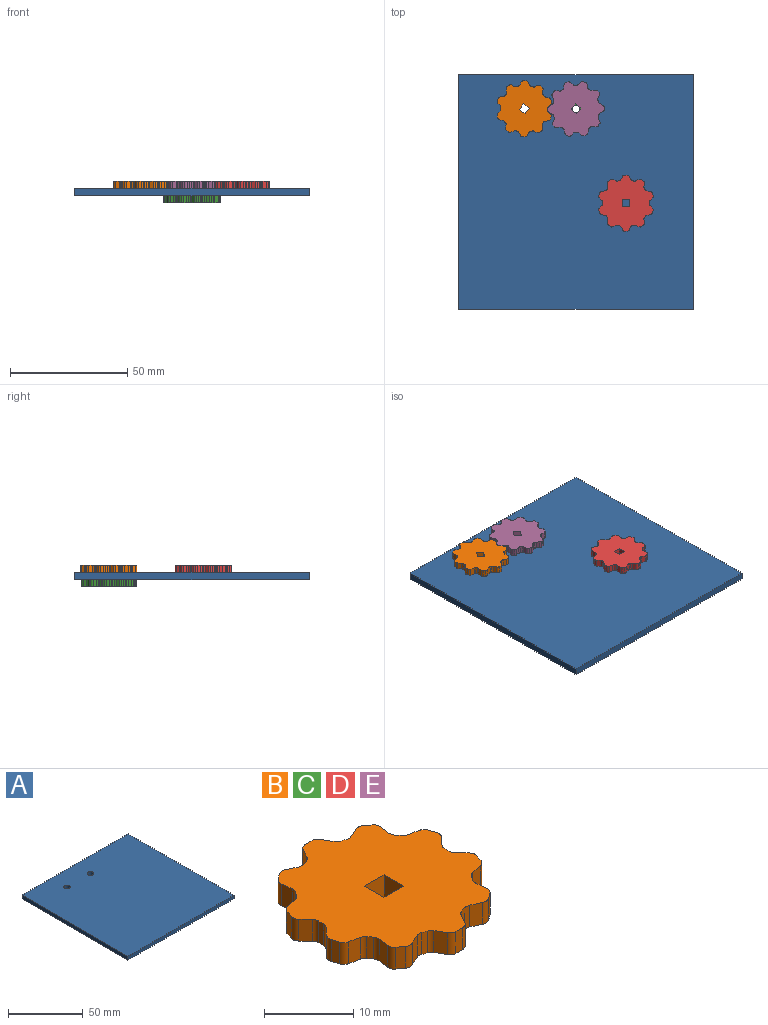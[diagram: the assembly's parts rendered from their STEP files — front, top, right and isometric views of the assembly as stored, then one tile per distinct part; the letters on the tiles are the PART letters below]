
ASSEMBLY  parts=5 mates=3
PART A: 8 faces, bbox 100x100x3 mm
  f0: plane 100x3mm, normal (1,0,0), area 300mm2, adj f1,f3,f4,f5
  f1: plane 100x3mm, normal (0,1,0), area 300mm2, adj f0,f2,f4,f5
  f2: plane 100x3mm, normal (-1,0,0), area 300mm2, adj f1,f3,f4,f5
  f3: plane 100x3mm, normal (0,-1,0), area 300mm2, adj f0,f2,f4,f5
  f4: plane 100x100mm, normal (0,0,1), area 9969.8mm2, adj f0,f1,f2,f3,f6,f7
  f5: plane 100x100mm, normal (0,0,-1), area 9969.8mm2, adj f0,f1,f2,f3,f6,f7
  f6: cylinder r=2.19mm len=4.38mm, axis (0,0,1), area 41.3mm2, adj f4,f5
  f7: cylinder r=2.19mm len=4.38mm, axis (0,0,1), area 41.3mm2, adj f4,f5
PART B: 86 faces, bbox 23.2x23.9x3 mm
  f0: cylinder r=10mm len=3mm, axis (0,0,-1), area 2.1mm2, adj f14,f15,f20,f84
  f1: cylinder r=10mm len=3mm, axis (0,0,-1), area 2.1mm2, adj f14,f15,f77,f83
  f2: cylinder r=10mm len=3mm, axis (0,0,-1), area 2.1mm2, adj f14,f15,f70,f76
  f3: cylinder r=10mm len=3mm, axis (0,0,-1), area 2.1mm2, adj f14,f15,f63,f69
  f4: cylinder r=10mm len=3mm, axis (0,0,-1), area 2.1mm2, adj f14,f15,f56,f62
  f5: cylinder r=10mm len=3mm, axis (0,0,-1), area 2.1mm2, adj f14,f15,f49,f55
  f6: cylinder r=10mm len=3mm, axis (0,0,-1), area 2.1mm2, adj f14,f15,f42,f48
  f7: cylinder r=10mm len=3mm, axis (0,0,-1), area 2.1mm2, adj f14,f15,f35,f41
  f8: cylinder r=10mm len=3mm, axis (0,0,-1), area 2.1mm2, adj f14,f15,f28,f34
  f9: cylinder r=10mm len=3mm, axis (0,0,-1), area 2.1mm2, adj f14,f15,f21,f27
  f10: plane 3.05x3mm, normal (0,-1,0), area 9.2mm2, adj f11,f13,f14,f15
  f11: plane 3.05x3mm, normal (-1,0,0), area 9.2mm2, adj f10,f12,f14,f15
  f12: plane 3.05x3mm, normal (0,1,0), area 9.2mm2, adj f11,f13,f14,f15
  f13: plane 3.05x3mm, normal (1,0,0), area 9.2mm2, adj f10,f12,f14,f15
  f14: plane 23.9x23.15mm, normal (0,0,1), area 372.8mm2, adj f0,f1,f2,f3,f4,f5,f6,f7
  f15: plane 23.9x23.15mm, normal (0,0,-1), area 372.8mm2, adj f0,f1,f2,f3,f4,f5,f6,f7
  f16: plane 3x1.06mm, normal (0,1,0), area 3.2mm2, adj f14,f15,f19,f22
  f17: plane 3x1.35mm, normal (-0.87,0.49,0), area 4.6mm2, adj f14,f15,f19,f20
  f18: plane 3x1.35mm, normal (0.87,0.49,0), area 4.6mm2, adj f14,f15,f21,f22
  f19: cylinder r=1mm len=3mm, axis (0,0,1), area 3.2mm2, adj f14,f15,f16,f17
  f20: cylinder r=1mm len=3mm, axis (0,0,-1), area 2.3mm2, adj f0,f14,f15,f17
  f21: cylinder r=1mm len=3mm, axis (0,0,-1), area 2.3mm2, adj f9,f14,f15,f18
  f22: cylinder r=1mm len=3mm, axis (0,0,-1), area 3.2mm2, adj f14,f15,f16,f18
  f23: plane 3x0.86mm, normal (0.59,0.81,0), area 3.2mm2, adj f14,f15,f26,f29
  f24: plane 3x1.4mm, normal (-0.42,0.91,0), area 4.6mm2, adj f14,f15,f26,f27
  f25: plane 3x1.53mm, normal (0.99,-0.12,0), area 4.6mm2, adj f14,f15,f28,f29
  f26: cylinder r=1mm len=3mm, axis (0,0,1), area 3.2mm2, adj f14,f15,f23,f24
  f27: cylinder r=1mm len=3mm, axis (0,0,-1), area 2.3mm2, adj f9,f14,f15,f24
  f28: cylinder r=1mm len=3mm, axis (0,0,-1), area 2.3mm2, adj f8,f14,f15,f25
  f29: cylinder r=1mm len=3mm, axis (0,0,-1), area 3.2mm2, adj f14,f15,f23,f25
  f30: plane 3x1.01mm, normal (0.95,0.31,0), area 3.2mm2, adj f14,f15,f33,f36
  f31: plane 3x1.51mm, normal (0.19,0.98,0), area 4.6mm2, adj f14,f15,f33,f34
  f32: plane 3x1.13mm, normal (0.73,-0.68,0), area 4.6mm2, adj f14,f15,f35,f36
  f33: cylinder r=1mm len=3mm, axis (0,0,1), area 3.2mm2, adj f14,f15,f30,f31
  f34: cylinder r=1mm len=3mm, axis (0,0,-1), area 2.3mm2, adj f8,f14,f15,f31
  f35: cylinder r=1mm len=3mm, axis (0,0,-1), area 2.3mm2, adj f7,f14,f15,f32
  f36: cylinder r=1mm len=3mm, axis (0,0,-1), area 3.2mm2, adj f14,f15,f30,f32
  f37: plane 3x1.01mm, normal (0.95,-0.31,0), area 3.2mm2, adj f14,f15,f40,f43
  f38: plane 3x1.13mm, normal (0.73,0.68,0), area 4.6mm2, adj f14,f15,f40,f41
  f39: plane 3x1.51mm, normal (0.19,-0.98,0), area 4.6mm2, adj f14,f15,f42,f43
  f40: cylinder r=1mm len=3mm, axis (0,0,1), area 3.2mm2, adj f14,f15,f37,f38
  f41: cylinder r=1mm len=3mm, axis (0,0,-1), area 2.3mm2, adj f7,f14,f15,f38
  f42: cylinder r=1mm len=3mm, axis (0,0,-1), area 2.3mm2, adj f6,f14,f15,f39
  f43: cylinder r=1mm len=3mm, axis (0,0,-1), area 3.2mm2, adj f14,f15,f37,f39
  f44: plane 3x0.86mm, normal (0.59,-0.81,0), area 3.2mm2, adj f14,f15,f47,f50
  f45: plane 3x1.53mm, normal (0.99,0.12,0), area 4.6mm2, adj f14,f15,f47,f48
  f46: plane 3x1.4mm, normal (-0.42,-0.91,0), area 4.6mm2, adj f14,f15,f49,f50
  f47: cylinder r=1mm len=3mm, axis (0,0,1), area 3.2mm2, adj f14,f15,f44,f45
  f48: cylinder r=1mm len=3mm, axis (0,0,-1), area 2.3mm2, adj f6,f14,f15,f45
  f49: cylinder r=1mm len=3mm, axis (0,0,-1), area 2.3mm2, adj f5,f14,f15,f46
  f50: cylinder r=1mm len=3mm, axis (0,0,-1), area 3.2mm2, adj f14,f15,f44,f46
  f51: plane 3x1.06mm, normal (0,-1,0), area 3.2mm2, adj f14,f15,f54,f57
  f52: plane 3x1.35mm, normal (0.87,-0.49,0), area 4.6mm2, adj f14,f15,f54,f55
  f53: plane 3x1.35mm, normal (-0.87,-0.49,0), area 4.6mm2, adj f14,f15,f56,f57
  f54: cylinder r=1mm len=3mm, axis (0,0,1), area 3.2mm2, adj f14,f15,f51,f52
  f55: cylinder r=1mm len=3mm, axis (0,0,-1), area 2.3mm2, adj f5,f14,f15,f52
  f56: cylinder r=1mm len=3mm, axis (0,0,-1), area 2.3mm2, adj f4,f14,f15,f53
  f57: cylinder r=1mm len=3mm, axis (0,0,-1), area 3.2mm2, adj f14,f15,f51,f53
  f58: plane 3x0.86mm, normal (-0.59,-0.81,0), area 3.2mm2, adj f14,f15,f61,f64
  f59: plane 3x1.4mm, normal (0.42,-0.91,0), area 4.6mm2, adj f14,f15,f61,f62
  f60: plane 3x1.53mm, normal (-0.99,0.12,0), area 4.6mm2, adj f14,f15,f63,f64
  f61: cylinder r=1mm len=3mm, axis (0,0,1), area 3.2mm2, adj f14,f15,f58,f59
  f62: cylinder r=1mm len=3mm, axis (0,0,-1), area 2.3mm2, adj f4,f14,f15,f59
  f63: cylinder r=1mm len=3mm, axis (0,0,-1), area 2.3mm2, adj f3,f14,f15,f60
  f64: cylinder r=1mm len=3mm, axis (0,0,-1), area 3.2mm2, adj f14,f15,f58,f60
  f65: plane 3x1.01mm, normal (-0.95,-0.31,0), area 3.2mm2, adj f14,f15,f68,f71
  f66: plane 3x1.51mm, normal (-0.19,-0.98,0), area 4.6mm2, adj f14,f15,f68,f69
  f67: plane 3x1.13mm, normal (-0.73,0.68,0), area 4.6mm2, adj f14,f15,f70,f71
  f68: cylinder r=1mm len=3mm, axis (0,0,1), area 3.2mm2, adj f14,f15,f65,f66
  f69: cylinder r=1mm len=3mm, axis (0,0,-1), area 2.3mm2, adj f3,f14,f15,f66
  f70: cylinder r=1mm len=3mm, axis (0,0,-1), area 2.3mm2, adj f2,f14,f15,f67
  f71: cylinder r=1mm len=3mm, axis (0,0,-1), area 3.2mm2, adj f14,f15,f65,f67
  f72: plane 3x1.01mm, normal (-0.95,0.31,0), area 3.2mm2, adj f14,f15,f75,f78
  f73: plane 3x1.13mm, normal (-0.73,-0.68,0), area 4.6mm2, adj f14,f15,f75,f76
  f74: plane 3x1.51mm, normal (-0.19,0.98,0), area 4.6mm2, adj f14,f15,f77,f78
  f75: cylinder r=1mm len=3mm, axis (0,0,1), area 3.2mm2, adj f14,f15,f72,f73
  f76: cylinder r=1mm len=3mm, axis (0,0,-1), area 2.3mm2, adj f2,f14,f15,f73
  f77: cylinder r=1mm len=3mm, axis (0,0,-1), area 2.3mm2, adj f1,f14,f15,f74
  f78: cylinder r=1mm len=3mm, axis (0,0,-1), area 3.2mm2, adj f14,f15,f72,f74
  f79: plane 3x0.86mm, normal (-0.59,0.81,0), area 3.2mm2, adj f14,f15,f82,f85
  f80: plane 3x1.53mm, normal (-0.99,-0.12,0), area 4.6mm2, adj f14,f15,f82,f83
  f81: plane 3x1.4mm, normal (0.42,0.91,0), area 4.6mm2, adj f14,f15,f84,f85
  f82: cylinder r=1mm len=3mm, axis (0,0,1), area 3.2mm2, adj f14,f15,f79,f80
  f83: cylinder r=1mm len=3mm, axis (0,0,-1), area 2.3mm2, adj f1,f14,f15,f80
  f84: cylinder r=1mm len=3mm, axis (0,0,-1), area 2.3mm2, adj f0,f14,f15,f81
  f85: cylinder r=1mm len=3mm, axis (0,0,-1), area 3.2mm2, adj f14,f15,f79,f81
PART C: same geometry as B
PART D: same geometry as B
PART E: same geometry as B
PLACE A t=(-0.54,-0.47,0.53)mm fixed
PLACE B rot(axis=(0,0,-1),37deg) t=(-22.54,34.95,3.53)mm
PLACE C rot(axis=(0,0,-1),96.4deg) t=(-0.54,34.95,-2.47)mm
PLACE D t=(20.74,-5.22,3.53)mm
PLACE E rot(axis=(0,0,1),55deg) t=(-0.54,34.95,3.53)mm
MATE revolute C.f0 <-> A.f6  axis (0,0,1) through (-0.54,34.95,-0.97)mm
MATE revolute E.f0 <-> A.f6  axis (0,0,-1) through (-0.54,34.95,2.03)mm
MATE revolute B.f0 <-> A.f7  axis (0,0,-1) through (-22.54,34.95,2.03)mm
